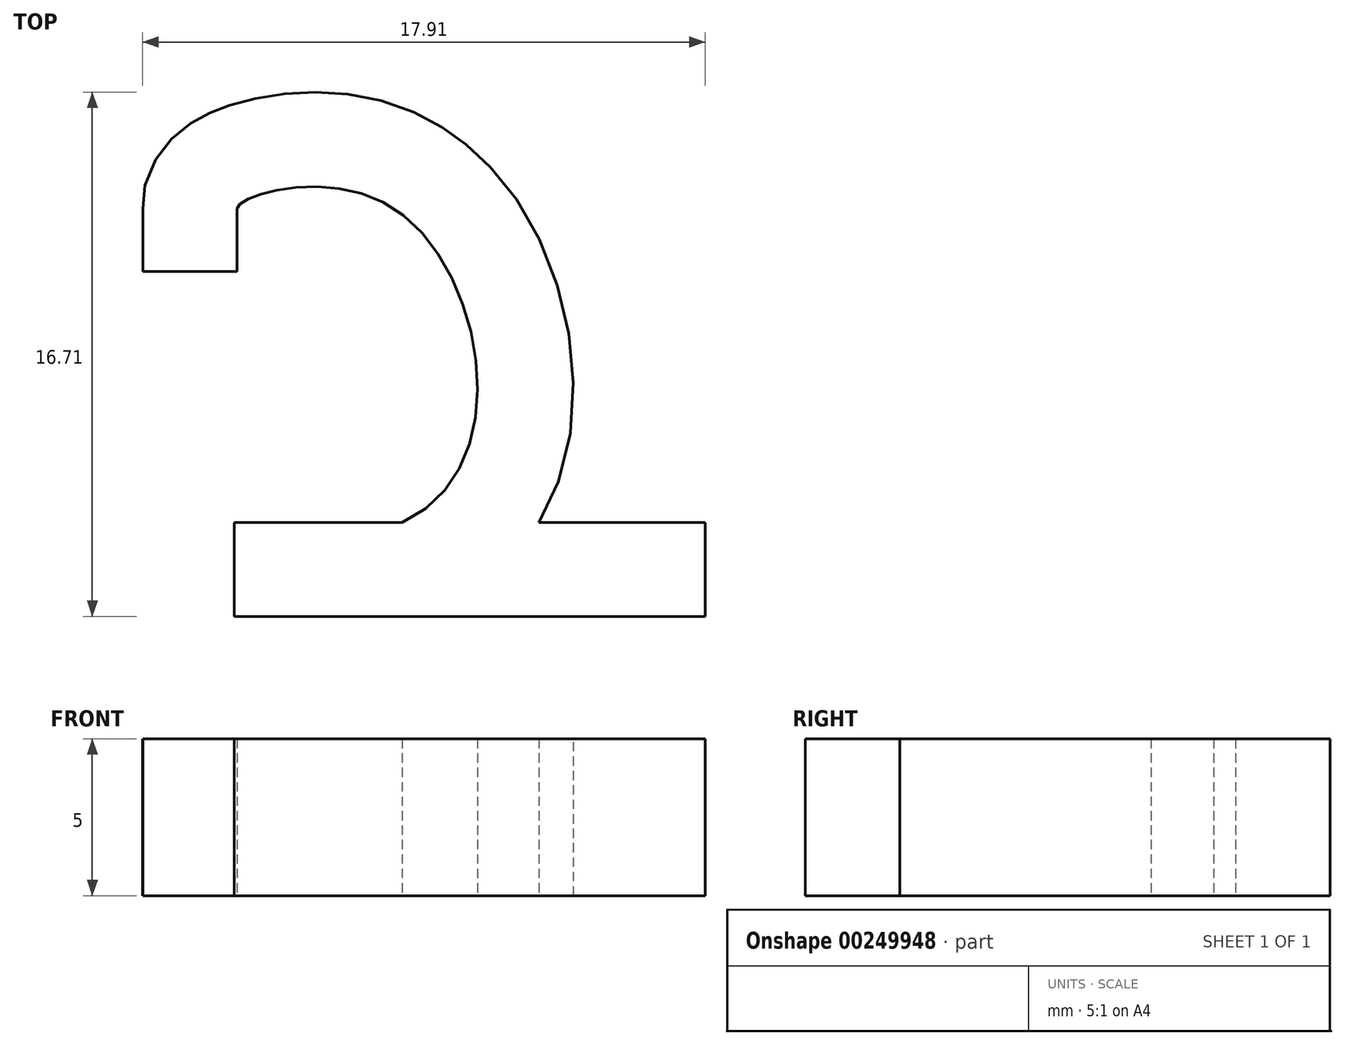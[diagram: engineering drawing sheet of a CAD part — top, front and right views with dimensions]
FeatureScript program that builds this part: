
annotation { "Feature Type Name" : "Feature", "Feature Type Description" : "" }
export const myFeature = defineFeature(function(context is Context, id is Id, definition is map)
    precondition{}
    {
        {
            var Q0;
            Q0=qCreatedBy(makeId("Top.planeOp"),FACE);
            var sketch = newSketch(context, id + "F0", { "sketchPlane" : qUnion([Q0])});
            skLineSegment(sketch, "E0.bottom", {"start": v(-5.1, 0) * mm, "end": v(9.9, 0) * mm});
            skLineSegment(sketch, "E0.top", {"start": v(-5.1, -3) * mm, "end": v(9.9, -3) * mm});
            skLineSegment(sketch, "E0.left", {"start": v(-5.1, 0) * mm, "end": v(-5.1, -3) * mm});
            skLineSegment(sketch, "E0.right", {"start": v(9.9, 0) * mm, "end": v(9.9, -3) * mm});
            skLineSegment(sketch, "E1", {"start": v(-8, 10) * mm, "end": v(-5, 10) * mm});
            skFitSpline(sketch, "E2", {"points": [v(-5, 10) * mm, v(0, 10) * mm, v(0.25, 0) * mm], "startDerivative": vector(0, 2.97) * mm, "endDerivative": vector(-19.3, -8.47) * mm});
            skFitSpline(sketch, "E3.0", {"points": [v(-8, 10) * mm, v(-8, 10.28) * mm, v(-7.93, 10.8) * mm, v(-7.7, 11.39) * mm, v(-7.43, 11.81) * mm, v(-7.1, 12.21) * mm, v(-6.75, 12.52) * mm, v(-6.4, 12.76) * mm, v(-6.1, 12.94) * mm, v(-5.8, 13.07) * mm, v(-5.53, 13.19) * mm, v(-5.15, 13.32) * mm, v(-4.66, 13.46) * mm, v(-4.04, 13.59) * mm, v(-3.38, 13.67) * mm, v(-2.66, 13.7) * mm, v(-1.9, 13.69) * mm, v(-1.11, 13.6) * mm, v(-0.28, 13.4) * mm, v(0.57, 13.1) * mm, v(1.29, 12.74) * mm, v(1.85, 12.38) * mm, v(2.37, 11.98) * mm, v(2.95, 11.44) * mm, v(3.75, 10.5) * mm, v(4.54, 9.2) * mm, v(5.2, 7.52) * mm, v(5.6, 5.74) * mm, v(5.7, 3.9) * mm, v(5.45, 2.01) * mm, v(4.86, 0.45) * mm, v(4.1, -0.73) * mm, v(3.12, -1.8) * mm, v(2.16, -2.44) * mm, v(1.46, -2.75) * mm]});
            skLineSegment(sketch, "E4.top", {"start": v(-8, 8) * mm, "end": v(-5, 8) * mm});
            skLineSegment(sketch, "E4.left", {"start": v(-8, 10) * mm, "end": v(-8, 8) * mm});
            skLineSegment(sketch, "E4.right", {"start": v(-5, 10) * mm, "end": v(-5, 8) * mm});
            skLineSegment(sketch, "E5", {"start": v(0.25, 0) * mm, "end": v(4.55, 0) * mm, "construction": true});
            skPoint(sketch, "E6", {"position": v(2.4, 0) * mm});
            skSolve(sketch);
        }
        {
            var Q0;
            Q0 = qSketchRegion(id + "F0", true);
            extrude(context, id + "F1", {"entities" : qUnion([Q0]), "depth" : 5 * mm, "offsetDistance" : 25 * mm});
        }
    });
